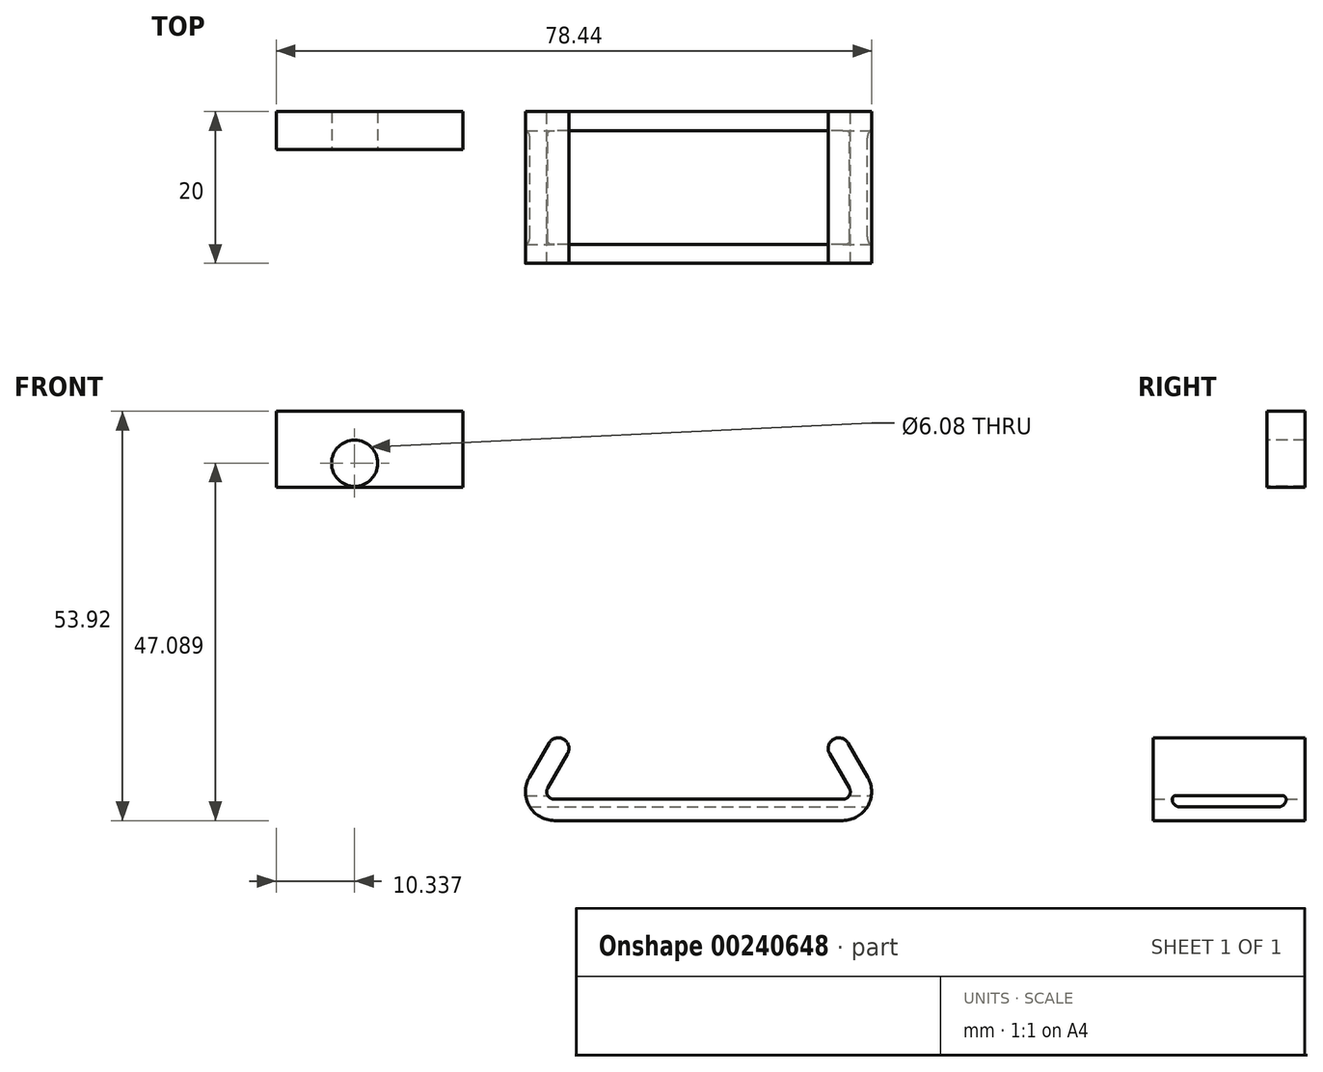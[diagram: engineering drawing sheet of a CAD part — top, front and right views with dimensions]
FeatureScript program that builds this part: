
annotation { "Feature Type Name" : "Feature", "Feature Type Description" : "" }
export const myFeature = defineFeature(function(context is Context, id is Id, definition is map)
    precondition{}
    {
        {
            var Q0;
            Q0=qCreatedBy(makeId("Front.planeOp"),FACE);
            var sketch = newSketch(context, id + "F0", { "sketchPlane" : qUnion([Q0])});
            skLineSegment(sketch, "E0", {"start": v(0, 0) * mm, "end": v(19, 0) * mm});
            skLineSegment(sketch, "E1", {"start": v(19.87, 1.5) * mm, "end": v(17.27, 6) * mm});
            skPoint(sketch, "E2.visualSharp", {"position": v(20.73, 0) * mm});
            skArc(sketch, "E2.filletArc", {"start": v(19, 0) * mm, "mid": v(19.87, 0.5) * mm, "end": v(19.87, 1.5) * mm});
            skLineSegment(sketch, "E3.0", {"start": v(22.3, 2.9) * mm, "end": v(19.7, 7.4) * mm});
            skArc(sketch, "E3.1", {"start": v(19, -2.8) * mm, "mid": v(22.3, -0.9) * mm, "end": v(22.3, 2.9) * mm});
            skLineSegment(sketch, "E3.2", {"start": v(0, -2.8) * mm, "end": v(19, -2.8) * mm});
            skArc(sketch, "E4", {"start": v(19.7, 7.4) * mm, "mid": v(17.78, 7.91) * mm, "end": v(17.27, 6) * mm});
            skLineSegment(sketch, "E5.MirrorCS", {"start": v(0, 0) * mm, "end": v(-19, 0) * mm});
            skLineSegment(sketch, "E6.MirrorCS", {"start": v(0, -2.8) * mm, "end": v(-19, -2.8) * mm});
            skArc(sketch, "E7.MirrorCS", {"start": v(-19, -2.8) * mm, "mid": v(-22.3, -0.9) * mm, "end": v(-22.3, 2.9) * mm});
            skArc(sketch, "E8.MirrorCS", {"start": v(-19, 0) * mm, "mid": v(-19.87, 0.5) * mm, "end": v(-19.87, 1.5) * mm});
            skLineSegment(sketch, "E9.MirrorCS", {"start": v(-19.87, 1.5) * mm, "end": v(-17.27, 6) * mm});
            skArc(sketch, "E10.MirrorCS", {"start": v(-19.7, 7.4) * mm, "mid": v(-17.78, 7.91) * mm, "end": v(-17.27, 6) * mm});
            skLineSegment(sketch, "E11.MirrorCS", {"start": v(-22.3, 2.9) * mm, "end": v(-19.7, 7.4) * mm});
            skSolve(sketch);
        }
        {
            var Q0;
            Q0 = qSketchRegion(id + "F0", true);
            extrude(context, id + "F1", {"entities" : qUnion([Q0]), "depth" : 20 * mm});
        }
        {
            var Q0;
            Q0=qCreatedBy(makeId("Right.planeOp"),FACE);
            var sketch = newSketch(context, id + "F2", { "sketchPlane" : qUnion([Q0])});
            skLineSegment(sketch, "E12.0", {"start": v(-20, 0) * mm, "end": v(0, 0) * mm, "construction": true});
            skLineSegment(sketch, "E13.0", {"start": v(-19.5, -1) * mm, "end": v(0, -1) * mm});
            skLineSegment(sketch, "E14.0", {"start": v(-19.5, 0.5) * mm, "end": v(0, 0.5) * mm});
            skLineSegment(sketch, "E15", {"start": v(-17.5, -1) * mm, "end": v(-17.5, 0.5) * mm});
            skLineSegment(sketch, "E16", {"start": v(-2.5, -1) * mm, "end": v(-2.5, 0.5) * mm});
            skSolve(sketch);
        }
        {
            var Q0;
            {var subQ0=sQuery(id+"F2.wireOp",EDGE,"E15");Q0=makeQuery(id+"F2.imprint","IMPRINT",FACE,{"disambiguationData":[TD([[makeQuery(id+"F2.imprint","IMPRINT",EDGE,{"derivedFrom":subQ0}),-1.0]])]});}
            extrude(context, id + "F3", {"entities" : qUnion([Q0]), "operationType" : NewBodyOperationType.REMOVE, "oppositeDirection" : true, "depth" : 50 * mm, "symmetric" : true});
        }
        {
            var Q0;
            Q0=makeQuery(id+"F3.boolean.opBoolean","COPY",EDGE,{"derivedFrom":makeQuery(id+"F3.opExtrude","SWEPT_EDGE",EDGE,{"disambiguationData":[OSD([sQuery(id+"F2.wireOp",EDGE,"E13.0"),sQuery(id+"F2.wireOp",EDGE,"E15")])]})});
            var Q1;
            Q1=makeQuery(id+"F3.boolean.opBoolean","COPY",EDGE,{"derivedFrom":makeQuery(id+"F3.opExtrude","SWEPT_EDGE",EDGE,{"disambiguationData":[OSD([sQuery(id+"F2.wireOp",EDGE,"E13.0"),sQuery(id+"F2.wireOp",EDGE,"E16")])]})});
            fillet(context, id + "F4", {"entities" : qUnion([Q0, Q1]), "radius" : 1 * mm, "tangentPropagation" : true, "allowEdgeOverflow" : false});
        }
        {
            var Q0;
            {var subQ0=sQuery(id+"F2.wireOp",EDGE,"E14.0");var subQ1=sQuery(id+"F2.wireOp",EDGE,"E15");Q0=makeQuery(id+"F3.boolean.opBoolean","COPY",EDGE,{"disambiguationData":[TD([makeQuery(id+"F1.opExtrude","SWEPT_FACE",FACE,{"disambiguationData":[OSD([sQuery(id+"F0.wireOp",EDGE,"E2.filletArc")])]})])],"derivedFrom":makeQuery(id+"F3.opExtrude","SWEPT_EDGE",EDGE,{"disambiguationData":[OSD([subQ0,subQ1])]})});}
            var Q1;
            {var subQ0=sQuery(id+"F2.wireOp",EDGE,"E14.0");var subQ1=sQuery(id+"F2.wireOp",EDGE,"E16");Q1=makeQuery(id+"F3.boolean.opBoolean","COPY",EDGE,{"disambiguationData":[TD([makeQuery(id+"F1.opExtrude","SWEPT_FACE",FACE,{"disambiguationData":[OSD([sQuery(id+"F0.wireOp",EDGE,"E2.filletArc")])]})])],"derivedFrom":makeQuery(id+"F3.opExtrude","SWEPT_EDGE",EDGE,{"disambiguationData":[OSD([subQ0,subQ1])]})});}
            var Q2;
            {var subQ0=sQuery(id+"F2.wireOp",EDGE,"E14.0");var subQ1=sQuery(id+"F2.wireOp",EDGE,"E15");Q2=makeQuery(id+"F3.boolean.opBoolean","COPY",EDGE,{"disambiguationData":[TD([makeQuery(id+"F1.opExtrude","SWEPT_FACE",FACE,{"disambiguationData":[OSD([sQuery(id+"F0.wireOp",EDGE,"E7.MirrorCS")])]})])],"derivedFrom":makeQuery(id+"F3.opExtrude","SWEPT_EDGE",EDGE,{"disambiguationData":[OSD([subQ0,subQ1])]})});}
            var Q3;
            {var subQ0=sQuery(id+"F2.wireOp",EDGE,"E14.0");var subQ1=sQuery(id+"F2.wireOp",EDGE,"E16");Q3=makeQuery(id+"F3.boolean.opBoolean","COPY",EDGE,{"disambiguationData":[TD([makeQuery(id+"F1.opExtrude","SWEPT_FACE",FACE,{"disambiguationData":[OSD([sQuery(id+"F0.wireOp",EDGE,"E7.MirrorCS")])]})])],"derivedFrom":makeQuery(id+"F3.opExtrude","SWEPT_EDGE",EDGE,{"disambiguationData":[OSD([subQ0,subQ1])]})});}
            fillet(context, id + "F5", {"entities" : qUnion([Q0, Q1, Q2, Q3]), "radius" : 0.5 * mm, "tangentPropagation" : true, "allowEdgeOverflow" : false});
        }
        {
            var Q0;
            Q0=qCreatedBy(makeId("Front.planeOp"),FACE);
            var sketch = newSketch(context, id + "F6", { "sketchPlane" : qUnion([Q0])});
            skLineSegment(sketch, "E17.bottom", {"start": v(-55.64, 51.12) * mm, "end": v(-31.01, 51.12) * mm});
            skLineSegment(sketch, "E17.top", {"start": v(-55.64, 41.1) * mm, "end": v(-31.01, 41.1) * mm});
            skLineSegment(sketch, "E17.left", {"start": v(-55.64, 51.12) * mm, "end": v(-55.64, 41.1) * mm});
            skLineSegment(sketch, "E17.right", {"start": v(-31.01, 51.12) * mm, "end": v(-31.01, 41.1) * mm});
            skSolve(sketch);
        }
        {
            var Q0;
            Q0 = qSketchRegion(id + "F6", true);
            extrude(context, id + "F7", {"entities" : qUnion([Q0]), "depth" : 5 * mm});
        }
        {
            var Q0;
            Q0=makeQuery(id+"F7.opExtrude","CAP_FACE",FACE,{"disambiguationData":[OSD([sQuery(id+"F6.wireOp",EDGE,"E17.bottom"),sQuery(id+"F6.wireOp",EDGE,"E17.top"),sQuery(id+"F6.wireOp",EDGE,"E17.left"),sQuery(id+"F6.wireOp",EDGE,"E17.right")])],"isStart":false});
            var sketch = newSketch(context, id + "F8", { "sketchPlane" : qUnion([Q0])});
            skCircle(sketch, "E18", {"center": v(-45.3, 44.29) * mm, "radius": 3.04 * mm});
            skSolve(sketch);
        }
        {
            var Q0;
            Q0 = qSketchRegion(id + "F8", true);
            extrude(context, id + "F9", {"entities" : qUnion([Q0]), "operationType" : NewBodyOperationType.REMOVE, "oppositeDirection" : true, "depth" : 25 * mm});
        }
    });
